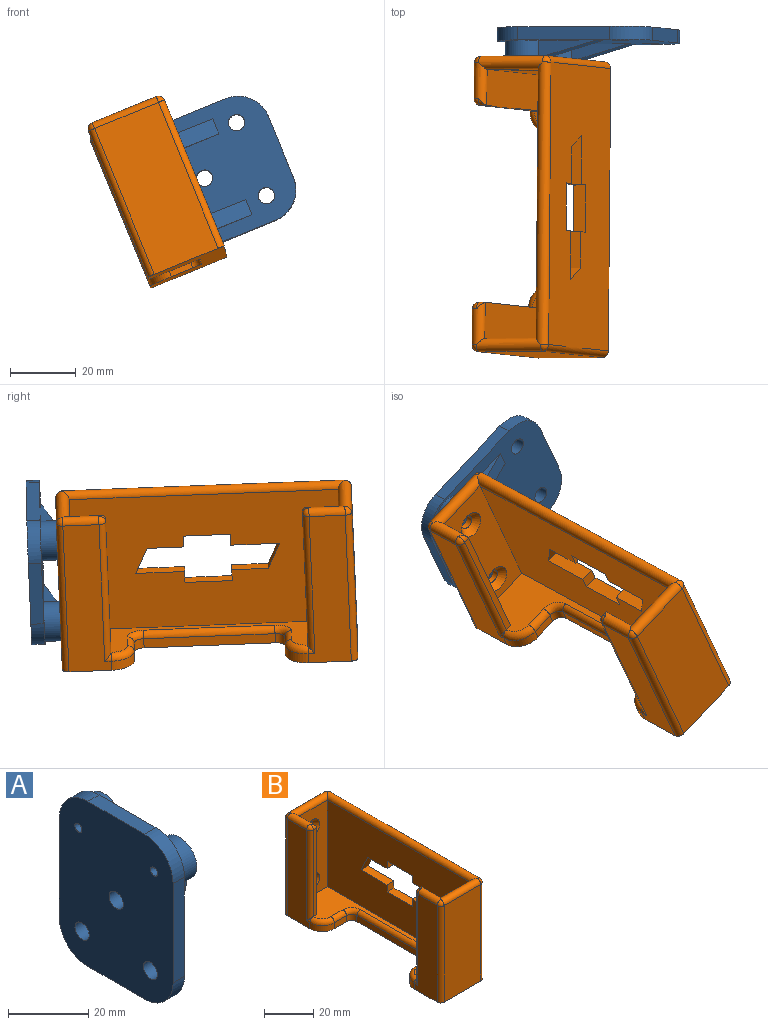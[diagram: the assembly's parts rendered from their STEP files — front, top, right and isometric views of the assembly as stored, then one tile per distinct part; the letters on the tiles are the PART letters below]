
ASSEMBLY  parts=2 mates=1
PART A: 25 faces, bbox 9x40x50.2 mm
  f0: cylinder r=6mm len=12mm, axis (-1,0,0), area 162.7mm2, adj f3,f13,f20,f21
  f1: cylinder r=6mm len=12mm, axis (-1,0,0), area 162.7mm2, adj f3,f12,f18,f19
  f2: plane 50.2x40mm, normal (-1,0,0), area 1853.4mm2, adj f4,f5,f6,f7,f8,f9,f10,f11
  f3: plane 50.2x40mm, normal (1,0,0), area 1450.3mm2, adj f0,f1,f4,f5,f6,f7,f9,f11
  f4: plane 20x4mm, normal (0,0,-1), area 80mm2, adj f2,f3,f14,f16
  f5: plane 20x4mm, normal (0,0,1), area 80mm2, adj f2,f3,f15,f17
  f6: plane 30.2x4mm, normal (0,-1,0), area 120.8mm2, adj f2,f3,f16,f17
  f7: plane 30.2x4mm, normal (0,1,0), area 120.8mm2, adj f2,f3,f14,f15
  f8: cylinder r=1.25mm len=9mm, axis (1,0,0), area 70.7mm2, adj f2,f13
  f9: cylinder r=2.5mm len=5mm, axis (1,0,0), area 62.8mm2, adj f2,f3
  f10: cylinder r=1.25mm len=9mm, axis (1,0,0), area 70.7mm2, adj f2,f12
  f11: cylinder r=2.5mm len=5mm, axis (1,0,0), area 62.8mm2, adj f2,f3
  f12: plane 12.5x12mm, normal (1,0,0), area 111.6mm2, adj f1,f10,f18,f19,f22
  f13: plane 12.5x12mm, normal (1,0,0), area 111.6mm2, adj f0,f8,f20,f21,f23
  f14: cylinder r=10mm len=10mm, axis (1,0,0), area 62.8mm2, adj f2,f3,f4,f7
  f15: cylinder r=10mm len=10mm, axis (-1,0,0), area 62.8mm2, adj f2,f3,f5,f7
  f16: cylinder r=10mm len=10mm, axis (-1,0,0), area 62.8mm2, adj f2,f3,f4,f6
  f17: cylinder r=10mm len=10mm, axis (1,0,0), area 62.8mm2, adj f2,f3,f5,f6
  f18: plane 19.05x5mm, normal (0,-1,0), area 50.2mm2, adj f1,f3,f12,f22
  f19: plane 19.05x5mm, normal (0,1,0), area 50.2mm2, adj f1,f3,f12,f22
  f20: plane 19.05x5mm, normal (0,-1,0), area 50.2mm2, adj f0,f3,f13,f23
  f21: plane 19.05x5mm, normal (0,1,0), area 50.2mm2, adj f0,f3,f13,f23
  f22: plane 18x5mm, normal (0.96,0,-0.27), area 93.4mm2, adj f3,f12,f18,f19
  f23: plane 18x5mm, normal (0.96,0,-0.27), area 93.4mm2, adj f3,f13,f20,f21
  f24: cylinder r=2.5mm len=5mm, axis (1,0,0), area 62.8mm2, adj f2,f3
PART B: 65 faces, bbox 25.6x90x50 mm
  f0: plane 48x13mm, normal (-1,0,0), area 534mm2, adj f1,f32,f45,f46,f52,f56
  f1: plane 90x25mm, normal (0,0,-1), area 1447.4mm2, adj f0,f4,f5,f6,f7,f14,f15,f16
  f2: plane 82x19mm, normal (0,0,1), area 664mm2, adj f3,f8,f9,f10,f11,f12,f13,f57
  f3: plane 43x11mm, normal (1,0,0), area 473mm2, adj f2,f8,f12,f39
  f4: plane 48x13mm, normal (-1,0,0), area 534mm2, adj f1,f31,f35,f37,f39,f64
  f5: plane 86x48mm, normal (1,0,0), area 3698.5mm2, adj f1,f17,f18,f19,f20,f21,f22,f23
  f6: plane 48x21mm, normal (0,-1,0), area 1008mm2, adj f1,f44,f45,f51
  f7: plane 48x21mm, normal (0,1,0), area 980.3mm2, adj f1,f29,f30,f37,f41,f42
  f8: plane 43x17mm, normal (0,-1,0), area 625.4mm2, adj f2,f3,f11,f42,f54,f55
  f9: plane 43x11mm, normal (1,0,0), area 473mm2, adj f2,f10,f13,f52
  f10: plane 43x17mm, normal (0,1,0), area 731mm2, adj f2,f9,f11,f51
  f11: plane 82x43mm, normal (-1,0,0), area 3096.5mm2, adj f2,f8,f10,f17,f18,f19,f20,f21
  f12: plane 43x2mm, normal (0,-1,0), area 86mm2, adj f2,f3,f35,f38
  f13: plane 43x2mm, normal (0,1,0), area 86mm2, adj f2,f9,f46,f53
  f14: plane 7x3mm, normal (0,-1,0), area 21mm2, adj f1,f31,f34,f62
  f15: plane 7x3mm, normal (0,1,0), area 21mm2, adj f1,f32,f33,f58
  f16: plane 40x3mm, normal (-1,0,0), area 120mm2, adj f1,f33,f34,f60
  f17: plane 14.88x4mm, normal (0,0,-1), area 59.5mm2, adj f5,f11,f18,f28
  f18: plane 4x3.57mm, normal (0,1,0), area 14.3mm2, adj f5,f11,f17,f19
  f19: plane 14.38x4mm, normal (0,0,-1), area 57.5mm2, adj f5,f11,f18,f20
  f20: plane 4x3.57mm, normal (0,-1,0), area 14.3mm2, adj f5,f11,f19,f21
  f21: plane 11.11x4mm, normal (0,0,-1), area 44.4mm2, adj f5,f11,f20,f22
  f22: plane 8.09x4mm, normal (0,-0.91,-0.42), area 35.7mm2, adj f5,f11,f21,f23
  f23: plane 14.88x4mm, normal (0,0,1), area 59.5mm2, adj f5,f11,f22,f24
  f24: plane 4x3.57mm, normal (0,-1,0), area 14.3mm2, adj f5,f11,f23,f25
  f25: plane 14.38x4mm, normal (0,0,1), area 57.5mm2, adj f5,f11,f24,f26
  f26: plane 4x3.57mm, normal (0,1,0), area 14.3mm2, adj f5,f11,f25,f27
  f27: plane 11.11x4mm, normal (0,0,1), area 44.4mm2, adj f5,f11,f26,f28
  f28: plane 8.09x4mm, normal (0,0.91,0.42), area 35.7mm2, adj f5,f11,f17,f27
  f29: cylinder r=2.1mm len=4.2mm, axis (0,1,0), area 26.4mm2, adj f7,f54
  f30: cylinder r=2.1mm len=4.2mm, axis (0,1,0), area 26.4mm2, adj f7,f55
  f31: cylinder r=7mm len=7mm, axis (0,0,-1), area 33mm2, adj f1,f4,f14,f63
  f32: cylinder r=7mm len=7mm, axis (0,0,1), area 33mm2, adj f0,f1,f15,f57
  f33: cylinder r=3mm len=3mm, axis (0,0,1), area 14.1mm2, adj f1,f15,f16,f59
  f34: cylinder r=3mm len=3mm, axis (0,0,-1), area 14.1mm2, adj f1,f14,f16,f61
  f35: cylinder r=2mm len=45mm, axis (0,0,-1), area 137.4mm2, adj f4,f12,f36,f64
  f36: sphere r=2mm, area 6.3mm2, adj f35,f38,f39
  f37: cylinder r=2mm len=48mm, axis (0,0,-1), area 150.8mm2, adj f1,f4,f7,f40
  f38: cylinder r=2mm len=2mm, axis (-1,0,0), area 4mm2, adj f12,f36,f39
  f39: cylinder r=2mm len=13mm, axis (0,1,0), area 69.1mm2, adj f3,f4,f36,f38,f40,f42
  f40: sphere r=2mm, area 6.3mm2, adj f37,f39,f42
  f41: cylinder r=2mm len=48mm, axis (0,0,1), area 150.8mm2, adj f1,f5,f7,f43
  f42: cylinder r=2mm len=21mm, axis (-1,0,0), area 123.9mm2, adj f7,f8,f39,f40,f43,f47
  f43: sphere r=2mm, area 6.3mm2, adj f41,f42,f47
  f44: cylinder r=2mm len=48mm, axis (0,0,-1), area 150.8mm2, adj f1,f5,f6,f48
  f45: cylinder r=2mm len=48mm, axis (0,0,1), area 150.8mm2, adj f0,f1,f6,f49
  f46: cylinder r=2mm len=45mm, axis (0,0,1), area 137.4mm2, adj f0,f13,f50,f56
  f47: cylinder r=2mm len=86mm, axis (0,1,0), area 532.4mm2, adj f5,f11,f42,f43,f48,f51
  f48: sphere r=2mm, area 6.3mm2, adj f44,f47,f51
  f49: sphere r=2mm, area 6.3mm2, adj f45,f51,f52
  f50: sphere r=2mm, area 6.3mm2, adj f46,f52,f53
  f51: cylinder r=2mm len=21mm, axis (1,0,0), area 123.9mm2, adj f6,f10,f47,f48,f49,f52
  f52: cylinder r=2mm len=13mm, axis (0,1,0), area 69.1mm2, adj f0,f9,f49,f50,f51,f53
  f53: cylinder r=2mm len=2mm, axis (1,0,0), area 4mm2, adj f13,f50,f52
  f54: cone r=2.1mm half-angle=45deg, axis (0,-1,0), area 55.1mm2, adj f8,f29
  f55: cone r=2.1mm half-angle=45deg, axis (0,-1,0), area 55.1mm2, adj f8,f30
  f56: cylinder r=2mm len=2mm, axis (0,-1,0), area 2.3mm2, adj f0,f46,f57
  f57: torus R=5mm, axis (0,0,1), area 31mm2, adj f2,f32,f56,f58
  f58: cylinder r=2mm len=7mm, axis (-1,0,0), area 22mm2, adj f2,f15,f57,f59
  f59: torus R=5mm, axis (0,0,1), area 18.4mm2, adj f2,f33,f58,f60
  f60: cylinder r=2mm len=40mm, axis (0,-1,0), area 125.7mm2, adj f2,f16,f59,f61
  f61: torus R=5mm, axis (0,0,1), area 18.4mm2, adj f2,f34,f60,f62
  f62: cylinder r=2mm len=7mm, axis (1,0,0), area 22mm2, adj f2,f14,f61,f63
  f63: torus R=5mm, axis (0,0,1), area 31mm2, adj f2,f31,f62,f64
  f64: cylinder r=2mm len=2mm, axis (0,-1,0), area 2.3mm2, adj f4,f35,f63
PLACE A rot(axis=(0.63,-0.65,-0.42),132.4deg) t=(47.69,24.37,70.66)mm
PLACE B rot(axis=(-0.1,-0.99,0),22.4deg) t=(38.73,13.44,18.79)mm
MATE pin_slot B.f30 <-> A.f0  axis (0.01,1,-0.04) through (12.67,14.84,49.48)mm
